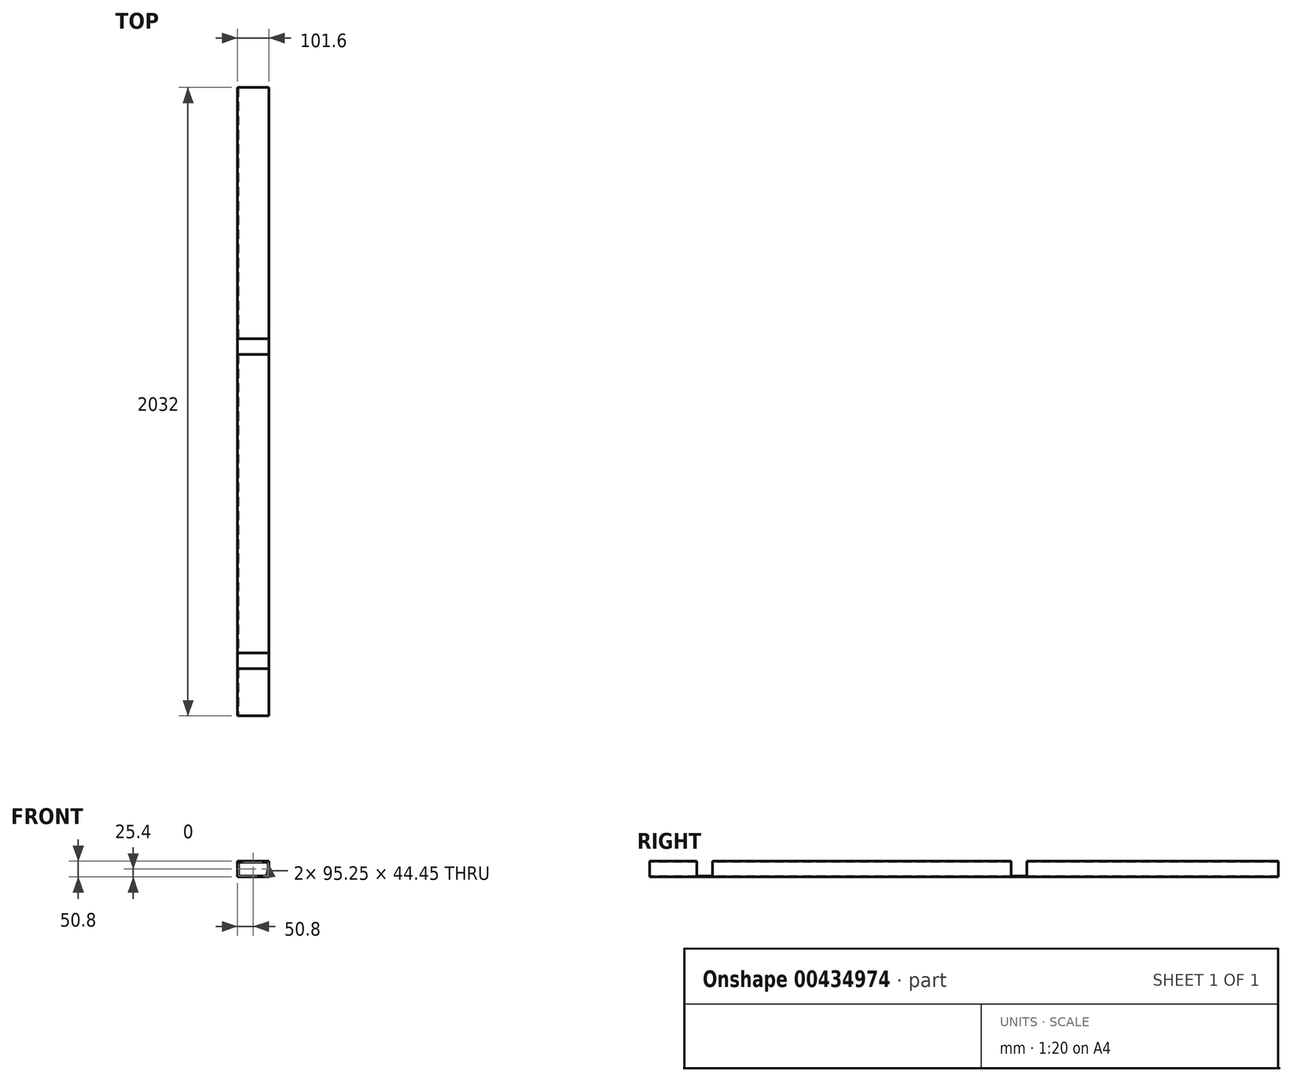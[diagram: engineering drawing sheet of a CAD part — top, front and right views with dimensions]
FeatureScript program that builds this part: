
annotation { "Feature Type Name" : "Feature", "Feature Type Description" : "" }
export const myFeature = defineFeature(function(context is Context, id is Id, definition is map)
    precondition{}
    {
        {
            var Q0;
            Q0=qCreatedBy(makeId("Front.planeOp"),FACE);
            var sketch = newSketch(context, id + "F0", { "sketchPlane" : qUnion([Q0])});
            skLineSegment(sketch, "E0.bottom", {"start": v(0, 0) * mm, "end": v(101.6, 0) * mm});
            skLineSegment(sketch, "E0.top", {"start": v(0, 50.8) * mm, "end": v(101.6, 50.8) * mm});
            skLineSegment(sketch, "E0.left", {"start": v(0, 0) * mm, "end": v(0, 50.8) * mm});
            skLineSegment(sketch, "E0.right", {"start": v(101.6, 0) * mm, "end": v(101.6, 50.8) * mm});
            skLineSegment(sketch, "E1.0", {"start": v(3.17, 3.18) * mm, "end": v(3.17, 47.63) * mm});
            skLineSegment(sketch, "E1.1", {"start": v(3.18, 3.18) * mm, "end": v(98.43, 3.18) * mm});
            skLineSegment(sketch, "E1.2", {"start": v(98.43, 3.18) * mm, "end": v(98.43, 47.63) * mm});
            skLineSegment(sketch, "E1.3", {"start": v(3.17, 47.63) * mm, "end": v(98.43, 47.63) * mm});
            skSolve(sketch);
        }
        {
            var Q0;
            Q0 = qSketchRegion(id + "F0", true);
            extrude(context, id + "F1", {"entities" : qUnion([Q0]), "oppositeDirection" : true, "depth" : 2032 * mm});
        }
        {
            var Q0;
            Q0=qCreatedBy(makeId("Right.planeOp"),FACE);
            var sketch = newSketch(context, id + "F2", { "sketchPlane" : qUnion([Q0])});
            skLineSegment(sketch, "E2.bottom", {"start": v(152.4, 50.8) * mm, "end": v(203.2, 50.8) * mm});
            skLineSegment(sketch, "E2.top", {"start": v(152.4, 3.17) * mm, "end": v(203.2, 3.17) * mm});
            skLineSegment(sketch, "E2.left", {"start": v(152.4, 50.8) * mm, "end": v(152.4, 3.17) * mm});
            skLineSegment(sketch, "E2.right", {"start": v(203.2, 50.8) * mm, "end": v(203.2, 3.17) * mm});
            skPoint(sketch, "E3.firstSnap0", {"position": v(177.8, 50.8) * mm});
            skLineSegment(sketch, "E3.bottom", {"start": v(1168.4, 50.8) * mm, "end": v(1219.2, 50.8) * mm});
            skLineSegment(sketch, "E3.top", {"start": v(1168.4, 3.17) * mm, "end": v(1219.2, 3.17) * mm});
            skLineSegment(sketch, "E3.left", {"start": v(1168.4, 50.8) * mm, "end": v(1168.4, 3.17) * mm});
            skLineSegment(sketch, "E3.right", {"start": v(1219.2, 50.8) * mm, "end": v(1219.2, 3.17) * mm});
            skPoint(sketch, "E4", {"position": v(1193.8, 50.8) * mm});
            skSolve(sketch);
        }
        {
            var Q0;
            Q0 = qSketchRegion(id + "F2", true);
            extrude(context, id + "F3", {"entities" : qUnion([Q0]), "operationType" : NewBodyOperationType.REMOVE, "endBound" : BoundingType.THROUGH_ALL, "depth" : 25.4 * mm});
        }
    });
